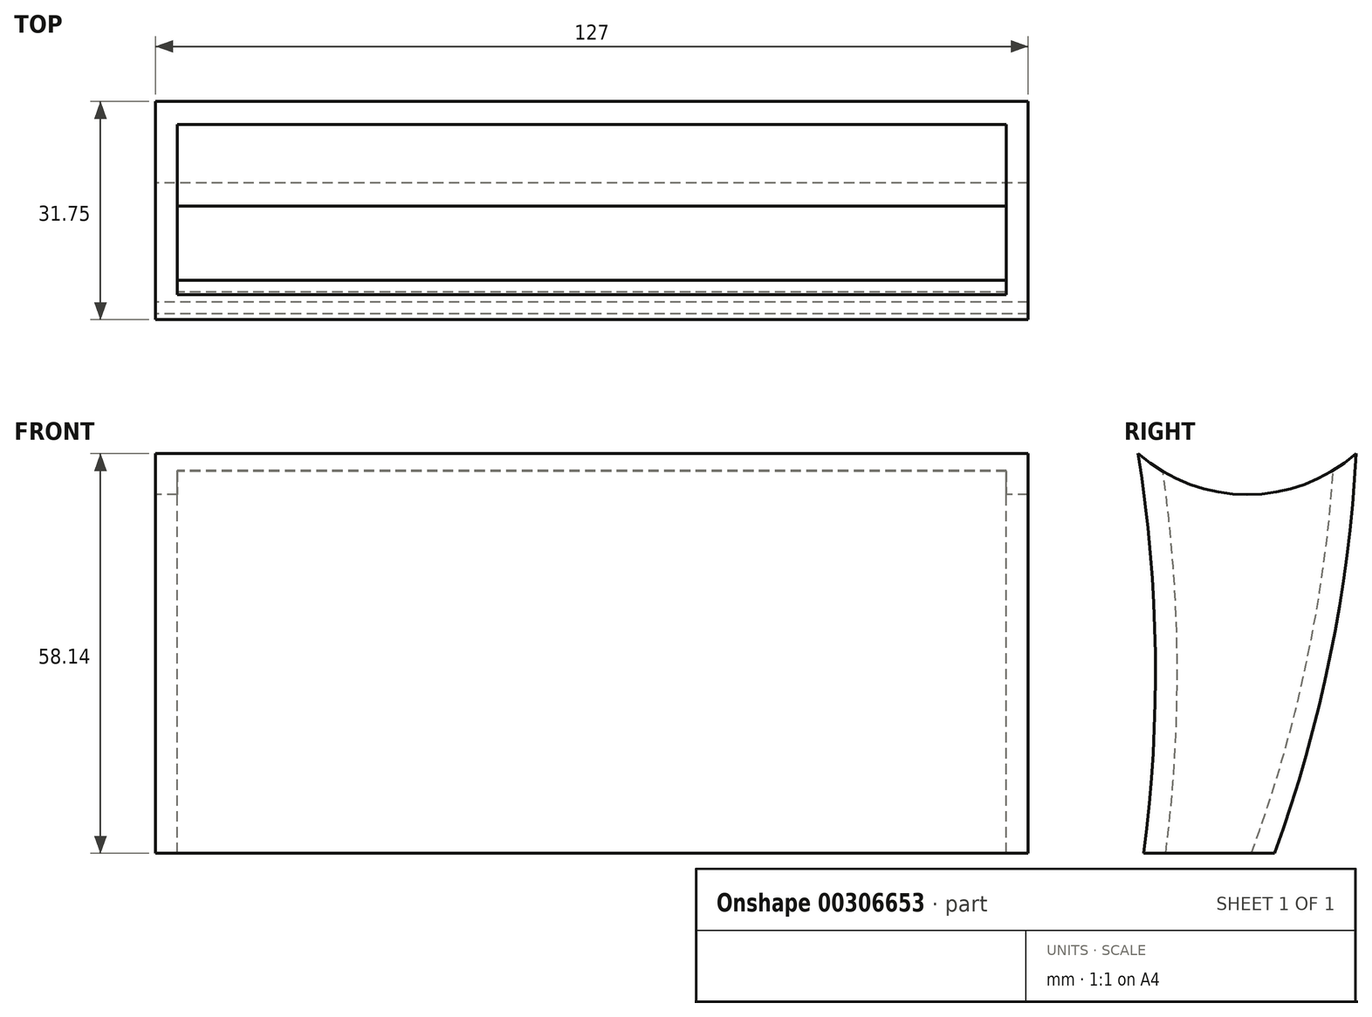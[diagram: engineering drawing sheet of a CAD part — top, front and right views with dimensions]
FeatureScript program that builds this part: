
annotation { "Feature Type Name" : "Feature", "Feature Type Description" : "" }
export const myFeature = defineFeature(function(context is Context, id is Id, definition is map)
    precondition{}
    {
        {
            var Q0;
            Q0=qCreatedBy(makeId("Right.planeOp"),FACE);
            var sketch = newSketch(context, id + "F0", { "sketchPlane" : qUnion([Q0])});
            skLineSegment(sketch, "E0.bottom", {"start": v(0, 0) * mm, "end": v(19.05, 0) * mm});
            skLineSegment(sketch, "E0.top", {"start": v(-0.83, 58.14) * mm, "end": v(30.92, 58.14) * mm});
            skArc(sketch, "E1", {"start": v(0, 0) * mm, "mid": v(1.68, 29.1) * mm, "end": v(-0.83, 58.14) * mm});
            skArc(sketch, "E2", {"start": v(19.05, 0) * mm, "mid": v(27.12, 28.64) * mm, "end": v(30.92, 58.14) * mm});
            skCircle(sketch, "E3", {"center": v(15.04, 76.31) * mm, "radius": 24.13 * mm});
            skSolve(sketch);
        }
        {
            var Q0;
            Q0=makeQuery(id+"F0.imprint","IMPRINT",FACE,{"disambiguationData":[TD([[makeQuery(id+"F0.imprint","IMPRINT",EDGE,{"derivedFrom":sQuery(id+"F0.wireOp",EDGE,"E0.bottom")}),1.0]])]});
            extrude(context, id + "F1", {"entities" : qUnion([Q0]), "depth" : 127 * mm});
        }
        {
            var Q0;
            Q0=makeQuery(id+"F1.opExtrude","SWEPT_FACE",FACE,{"disambiguationData":[OSD([sQuery(id+"F0.wireOp",EDGE,"E0.bottom")])]});
            var Q1;
            Q1=makeQuery(id+"F1.opExtrude","SWEPT_FACE",FACE,{"disambiguationData":[OSD([sQuery(id+"F0.wireOp",EDGE,"E3")])]});
            shell(context, id + "F2", {"entities" : qUnion([Q0, Q1]), "thickness" : 3.17 * mm});
        }
    });
